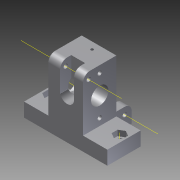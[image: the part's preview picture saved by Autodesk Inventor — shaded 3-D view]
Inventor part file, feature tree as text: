
AUTODESK INVENTOR PART (.ipt)
format: ipt  version: 2012 (Build 160160000, 160)  size: 297,984 bytes
history: native  units: mm
features: hole x11, sketch x10, extrude x7, other x4, fillet x2, plane x1, projected_geometry x1
ambient origin geometry x8: Origin, YZ Plane, XZ Plane, XY Plane, X Axis, Y Axis, Z Axis, Center Point
bodies: Solid1 (feature_tree)
feature tree (36):
  extrude  "Extrusion1"  Depth=24.0mm
  hole  "Hole1"  [1 undecoded]
  hole  "Hole2"  [1 undecoded]
  other  "Work Axis1"
  other  "Work Axis2"
  extrude  "Extrusion2"  Depth=7.5mm
  hole  "Hole3"  [1 undecoded]
  hole  "Hole4"  [1 undecoded]
  extrude  "Extrusion3"  Depth=6.0mm
  hole  "Hole5"  [1 undecoded]
  fillet  "Fillet1"  Radius=12.5mm
  extrude  "Extrusion4"  Depth=13.0mm
  hole  "Hole6"  [1 undecoded]
  hole  "Hole7"  [1 undecoded]
  hole  "Hole8"  [1 undecoded]
  hole  "Hole9"  [1 undecoded]
  hole  "Hole10"  [1 undecoded]
  plane  "Work Plane1"
  extrude  "Extrusion5"  Depth=3.0mm
  extrude  "Extrusion6"  Depth=19.0mm
  extrude  "Extrusion7"  [1 undecoded]
  hole  "Hole11"  [1 undecoded]
  sketch  "Sketch11"  dims[d46=11.0mm d47=25.0mm d48=12.5mm d49=13.0mm d50=13.0mm d51=0.0mm d52=5.0mm d53=6.0mm d54=3.0mm d55=6.0mm d56=4.0mm d57=2.0mm d58=90.0deg d59=0.2mm d60=20.594885mm d61=5.0mm d62=38.0mm d63=0.0mm d64=19.0mm d65=12.0mm d66=12.5mm d67=6.0mm d68=4.0mm d69=2.0mm d70=90.0deg d71=5.1mm d72=20.594885mm d102=10.0mm d103=10.0mm d75=23.0mm d76=6.0mm d77=4.0mm d78=2.0mm d79=90.0deg d80=3.0mm d81=20.594885mm d84=12.0mm d85=5.0mm d86=3.0mm d87=6.0mm d88=4.0mm d89=2.0mm d90=90.0deg d91=0.2mm d92=20.594885mm d93=12.0mm d94=33.0mm d95=3.0mm d96=6.0mm d97=4.0mm d98=2.0mm d99=90.0deg d100=0.2mm d101=20.594885mm d104=8.0mm d105=15.0mm d106=3.0mm d107=19.0mm d108=10.0mm d109=6.0mm d110=4.0mm d111=2.0mm d112=90.0deg d113=10.0mm d114=20.594885mm d115=-8.0mm d116=12.0mm d117=10.0mm d118=0.0mm d119=6.0mm d120=16.0mm d121=10.0mm d122=0.0mm d123=10.0mm d124=8.0mm d125=20.0mm d126=0.0mm d127=4.0mm d128=5.0mm d129=3.0mm d130=6.0mm d131=4.0mm d132=2.0mm d133=90.0deg d134=0.2mm d135=20.594885mm d138=21.0mm d139=5.0mm d140=4.0mm d141=5.0mm d144=1.0mm d145=1.0mm]
  other  "Work Axis3"
  other  "Work Axis4"
  fillet  "Fillet2"  Radius=10.0mm
  sketch  "Sketch1"  dims[d0=60.0mm d1=24.0mm]
  sketch  "Sketch2"  dims[d2=10.0mm d3=0.0mm d4=5.0mm d5=10.0mm]
  sketch  "Sketch3"  dims[d6=4.5mm d7=6.0mm d8=4.0mm d9=2.0mm d10=90.0deg d11=8.0mm d12=20.594885mm d13=5.0mm d14=10.0mm]
  sketch  "Sketch4"  dims[d15=4.5mm d16=6.0mm d17=4.0mm d18=2.0mm d19=90.0deg d20=8.0mm d21=20.594885mm d22=7.5mm]
  sketch  "Sketch5"  dims[d23=7.5mm d24=4.0mm d25=0.0mm]
  sketch  "Sketch6"  dims[d26=5.0mm]
  sketch  "Sketch7"  dims[d27=16.0mm d28=6.0mm d29=4.0mm d30=2.0mm d31=90.0deg d32=5.1mm d33=0.0mm]
  projected_geometry  "Projected Loop1"
  sketch  "Sketch8"  dims[d166=10.0mm d167=10.0mm d36=2.0mm d37=6.0mm d38=4.0mm d39=2.0mm d40=90.0deg d41=0.2mm d42=20.594885mm d43=6.0mm]
  sketch  "Sketch9"  dims[d44=11.0mm d45=6.0mm]
note: 12 required parameter values undecoded (feature->parameter linkage not recoverable at this tier; creation-order binding heuristic only, values carry confidence <= 0.55)
